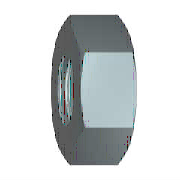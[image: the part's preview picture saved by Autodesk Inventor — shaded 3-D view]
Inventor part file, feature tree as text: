
AUTODESK INVENTOR PART (.ipt)
format: ipt  version: 2022 (Build 260153000, 153)  size: 163,328 bytes
history: native  units: mm (DEFAULTED — no unit token found)
features: sketch x3, other x2, extrude x1, hole x1, plane x1
ambient origin geometry x7: Origin, YZ Plane, XZ Plane, X Axis, Y Axis, Z Axis, Center Point
bodies: Solid1 (feature_tree)
feature tree (8):
  extrude  "Базовый элемент"  Depth=15.011107mm
  other  "Фаска1"
  hole  "Резьба"  [1 undecoded]
  other  "Work Axis1"
  plane  "Work Plane1"
  sketch  "Эскиз1"
  sketch  "Эскиз2"
  sketch  "Эскиз3"
note: 1 required parameter value undecoded (feature->parameter linkage not recoverable at this tier; creation-order binding heuristic only, values carry confidence <= 0.55)
